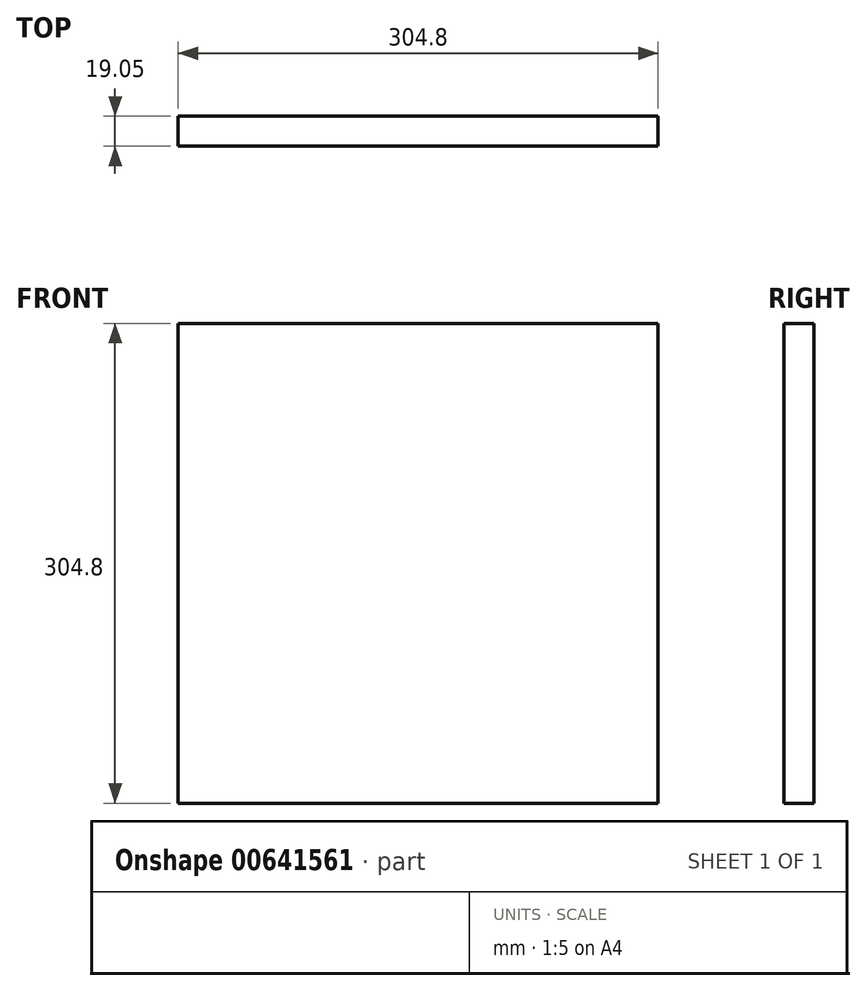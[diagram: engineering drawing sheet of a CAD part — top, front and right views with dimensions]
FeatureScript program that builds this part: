
annotation { "Feature Type Name" : "Feature", "Feature Type Description" : "" }
export const myFeature = defineFeature(function(context is Context, id is Id, definition is map)
    precondition{}
    {
        {
            var Q0;
            Q0=qCreatedBy(makeId("Front.planeOp"),FACE);
            var sketch = newSketch(context, id + "F0", { "sketchPlane" : qUnion([Q0])});
            skLineSegment(sketch, "E0", {"start": v(-175.07, 140.96) * mm, "end": v(129.73, 140.96) * mm});
            skLineSegment(sketch, "E1", {"start": v(129.73, 140.96) * mm, "end": v(129.73, -163.84) * mm});
            skLineSegment(sketch, "E2", {"start": v(129.73, -163.84) * mm, "end": v(-175.07, -163.84) * mm});
            skLineSegment(sketch, "E3", {"start": v(-175.07, -163.84) * mm, "end": v(-175.07, 140.96) * mm});
            skSolve(sketch);
        }
        {
            var Q0;
            Q0=makeQuery(id+"F0.imprint","IMPRINT",FACE,{"disambiguationData":[TD([[makeQuery(id+"F0.imprint","IMPRINT",EDGE,{"derivedFrom":sQuery(id+"F0.wireOp",EDGE,"E0")}),-1.0]])]});
            extrude(context, id + "F1", {"entities" : qUnion([Q0]), "depth" : 19.05 * mm, "offsetDistance" : 25.4 * mm});
        }
    });
